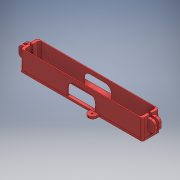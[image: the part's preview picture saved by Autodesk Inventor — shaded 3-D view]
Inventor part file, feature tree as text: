
AUTODESK INVENTOR PART (.ipt)
format: ipt  version: 2017 (Build 210142000, 142)  size: 564,736 bytes
history: native  units: mm
features: sketch x7, extrude x5, fillet x4, hole x2, mirror x2, projected_geometry x2
ambient origin geometry x8: Origin, YZ Plane, XZ Plane, XY Plane, X Axis, Y Axis, Z Axis, Center Point
bodies: Solid1 (feature_tree)
feature tree (22):
  extrude  "Extrusion1"  Depth=17.0mm
  extrude  "Extrusion2"  Depth=3.0mm TaperAngle=0.0deg
  extrude  "Extrusion3"  Depth=8.0mm
  fillet  "Fillet1"  Radius=4.0mm
  hole  "Hole1"  [1 undecoded]
  mirror  "Mirror1"
  mirror  "Mirror2"
  fillet  "Fillet2"  Radius=2.0mm
  extrude  "Extrusion4"  Depth=10.0mm TaperAngle=0.0deg
  fillet  "Fillet3"  Radius=5.25mm
  extrude  "Extrusion5"  Depth=2.75mm
  fillet  "Fillet4"  Radius=40.0mm
  hole  "Hole2"  [1 undecoded]
  sketch  "Sketch1"  dims[d0=159.0mm d1=17.0mm]
  sketch  "Sketch2"  dims[d2=4.0mm d3=3.0mm d4=0.0mm]
  projected_geometry  "Projected Loop1"
  sketch  "Sketch3"  dims[d5=8.0mm d6=8.0mm d7=4.0mm]
  sketch  "Sketch4"  dims[d8=166.0mm d9=21.0mm d10=2.0mm]
  projected_geometry  "Projected Loop2"
  sketch  "Sketch5"  dims[d11=25.5mm d12=-0.174533mm d14=10.0mm d15=0.0mm d16=5.25mm]
  sketch  "Sketch6"  dims[d17=2.3mm d18=6.0mm d19=4.0mm d20=2.0mm d21=90.0deg d22=8.0mm d23=20.594885mm d24=2.75mm d25=40.0mm]
  sketch  "Sketch7"  dims[d26=10.0mm d27=0.0mm d28=9.5mm d29=2.0mm d30=64.0mm d31=5.0mm d32=4.0mm d33=4.0mm d34=4.0mm d35=10.0mm d36=0.0mm d38=5.0mm d39=4.0mm d40=5.75mm d42=64.0mm d43=4.0mm d44=4.0mm d45=4.0mm d46=2.3mm d47=6.0mm d48=4.0mm d49=2.0mm d50=90.0deg d51=8.0mm d52=20.594885mm d53=12.5mm d54=12.0mm d55=12.5mm]
note: 2 required parameter values undecoded (feature->parameter linkage not recoverable at this tier; creation-order binding heuristic only, values carry confidence <= 0.55)
